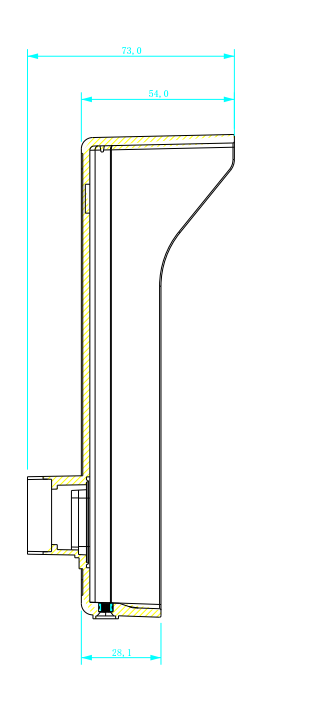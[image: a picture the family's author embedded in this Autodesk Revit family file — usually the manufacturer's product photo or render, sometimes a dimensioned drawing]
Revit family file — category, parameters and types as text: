
# Revit family: SP-03_with_SP-SP
name_source: partatom
category: Устройства связи
units: mm (PartAtom-declared; Revit-internal decimal feet)

## family parameters
Всегда вертикально = Нет
На основе рабочей плоскости = Да
Общий = Да
При загрузке вырезать с полостями = Нет
Размер круглого соединителя = Использовать диаметр
Сохранять ориентацию аннотаций = Нет
Тип детали = Нормальный
Точка принадлежности помещению = Нет

## types (1)
- SP-03 с аудиотрубкой SP-SP
    ADSK_URL документации изделия = https://wiki.bas-ip.com
    ADSK_URL страницы изделия = https://www.bas-ip.ru and https://www.bas-ip.ru
    ADSK_Версия Revit = Revit 2020
    ADSK_Единица измерения = шт
    ADSK_Завод-изготовитель = BAS-IP
    ADSK_Классификация нагрузок = Абонентское аудиоустройство
    ADSK_Количество фаз = 1
    ADSK_Коэффициент мощности = 0.9
    ADSK_Марка = SP-03 с аудиотрубкой SP-SP
    ADSK_Наименование = Абонентское аудиоустройство SP-03 с аудиотрубкой SP-SP
    ADSK_Наименование краткое = SP-03 с аудиотрубкой SP-SP
    ADSK_Напряжение = 12 В
    ADSK_Номинальная мощность = 6 Вт
    ADSK_Полная мощность = 6 В·А
    ADSK_Размер_Длина = 184 мм
    ADSK_Размер_Толщина = 28 мм
    ADSK_Размер_Ширина = 166 мм
    BIM library = https://bimlib.ru
    URL = https://www.bas-ip.ru
    Аудиотрубка SP-SP, размеры = 184x60 мм
    Вызов лифта = Есть
    Вызов на монитор консьержа = Есть
    Габаритные размеры = 184×166×28 мм
    Группа модели = Абонентское аудиоустройство SP-03 с аудиотрубкой SP-SP
    Дополнительная функция = Подключение дверного звонка
    Изготовитель = BAS-IP
    Изображение типоразмера = <Нет>
    Количество клавиш управления = 6
    Количество поддерживаемых учетных записей VoIP = 1
    Количество уровней громкости = 6
    Корпус = Пластик
    Материал корпуса = Материал белый
    Метод приемо-передачи аудиосигнала = Full Duplex
    Метод установки = Настенная
    Описание = Абонентское аудиоустройство SP-03 - Абонентское IP аудио устройство с поддержкой SIP, P2P и внутреннего протокола BAS-IP. Дополнителная аудиотрубка, которая подключается непосредственно к абонентскому аудиоустройству SP-03. Это решение идеально подходит для тех, кто желает конфиденциальности в разговорах.
    Открытие замка вызываемой панели = Есть
    Отметка по умолчанию = 0 мм
    Переадресация звонка = Есть
    Питание = PoE, +12 В (+11% -6%)
    Поддержка внутреннего протокола BAS-IP = Есть
    Поддержка протокола SIP 2.0 = Есть
    Подключение к сети = 1 PoE порт IEEE 802.3af
    Режим "Без звука" = Есть
    Режим "Не беспокоить" = Есть
    Способ настройки и программирования = WEB-интерфейс
    Тип поддерживаемого протокола = IPv4
    Тип поддерживаемых кодеков = G.711μ/A
    Трехцветный световой индикатор = Есть
    Цветовое решение = Белый, черный
